# Revit family: T-604_Ciclon CC
name_source: partatom
category: Plumbing Fixtures
revit_build: Autodesk Revit 2015 (Build: 20140606_1530(x64)
units: mm (PartAtom-declared; Revit-internal decimal feet)

## types (3) — shared parameters
Amax = 200 mm  [stored 0.656168 ft]
Amin = 75 mm
Apparent power = 200 VA
Certificates = http://www.jimten.com
"
Cistern = Jimten_Cistern
Depht Max = 220 mm  [stored 0.721785 ft]
Depht Min = 177 mm  [stored 0.580709 ft]
Description = CONCEALED CISTERN WITH SANITARY MACERATOR FOR A BATHROOM
Diameter Cistern = 40 mm  [stored 0.131234 ft]
Diameter Impulsion = 32 mm  [stored 0.104987 ft]
Diameter Side inlet L = 40 mm  [stored 0.131234 ft]
Diameter Side inlet R = 40 mm  [stored 0.131234 ft]
Diameter Side inlet T = 40 mm  [stored 0.131234 ft]
Diameter WC = 80 mm  [stored 0.262467 ft]
Flowrate = 1.7 L/s
Frame_Principal material = Jimten_Frame Blue
Frame_Secondary material = Jimten_Frame Steel
Inlets = 3x Ø40 mm
Load classification = Electrical appliances
Manufacturer = Jimten
MaxPumping Height = 6 m vertical
Model = T-604CC CICLON CC
Network = 220-240 VAC 50HZ
Number of poles = 1
Outlet = 1 x Ø32mm
Power = 470 W
Sanitary Appliance = No
Sanitary macerator = Jimten_Macerator
Type Comments = EASY MAINTENANCE THANKS TO ITS CASET SYSTEM. SILENT.
U.Outlet Bidet-Shower = 2
U.Outlet Wash basin = 1
Voltage = 230 V
WC = Yes
WFU = 2
Widht = 500 mm  [stored 1.64042 ft]
zero-valued in all types: Cost

## per-type parameters (varying)
| type | Panel | Panel_Material | Reference | URL |
| T-604 CC White | Yes | Jimten_Panel White | 75902 | http://www.jimten.com
" |
| T-604 CC Black | Yes | Jimten_Panel Black | 75903 | http://www.jimten.com
" |
| T-604 CC | No | Jimten_Frame Steel | 75901 | http://www.jimten.com |

note: [stored X ft] marks values corroborated as IEEE doubles in the binary element streams (Revit-internal decimal feet)

## geometry (parser evidence)
native form markers: Sweep x9
no freeform markers — native parametric forms only
